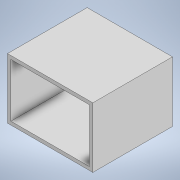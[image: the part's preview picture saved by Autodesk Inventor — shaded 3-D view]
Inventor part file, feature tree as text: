
AUTODESK INVENTOR PART (.ipt)
format: ipt  version: 2021 (Build 250183000, 183)  size: 194,560 bytes
history: native  units: mm
features: extrude x3, sketch x3, projected_geometry x2
ambient origin geometry x8: Origin, YZ Plane, XZ Plane, XY Plane, X Axis, Y Axis, Z Axis, Center Point
bodies: Solid2 (feature_tree), Solid1 (feature_tree)
feature tree (8):
  extrude  "Extrusion1"  Depth=3.0mm TaperAngle=0.0deg
  extrude  "Extrusion2"  [1 undecoded]
  extrude  "Extrusion3"  [1 undecoded]
  sketch  "Sketch1"  dims[d0=3.0mm d1=0.0mm d3=3.0mm d4=0.0mm]
  projected_geometry  "Projected Loop1"
  sketch  "Sketch2"  dims[d5=30.0mm d6=0.0mm]
  projected_geometry  "Projected Loop2"
  sketch  "Sketch3"
note: 2 required parameter values undecoded (feature->parameter linkage not recoverable at this tier; creation-order binding heuristic only, values carry confidence <= 0.55)
